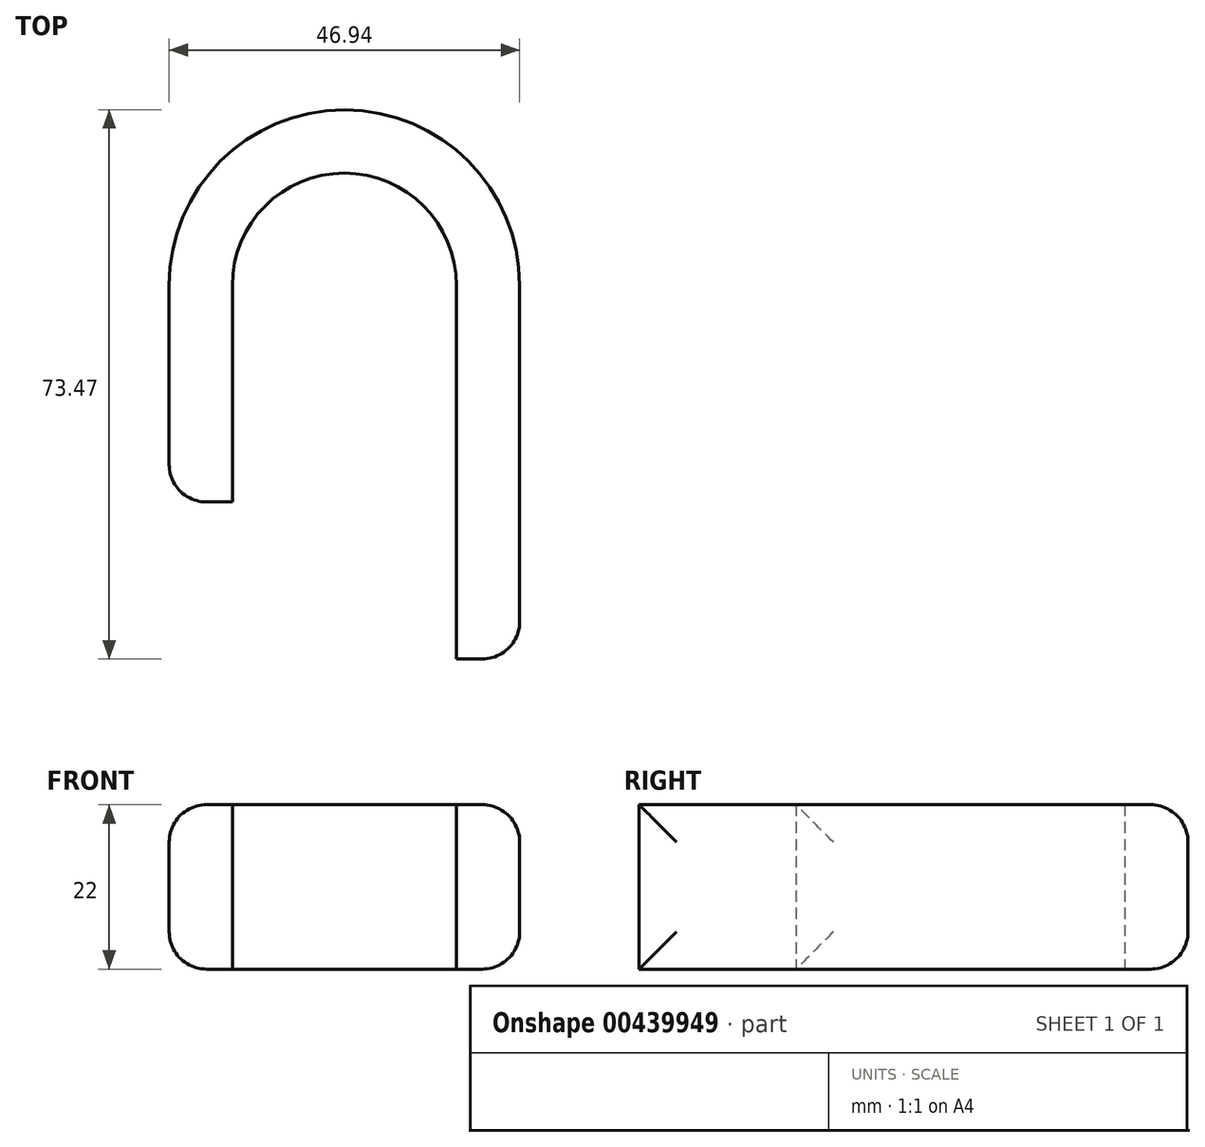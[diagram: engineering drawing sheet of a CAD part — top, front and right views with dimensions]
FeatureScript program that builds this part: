
annotation { "Feature Type Name" : "Feature", "Feature Type Description" : "" }
export const myFeature = defineFeature(function(context is Context, id is Id, definition is map)
    precondition{}
    {
        {
            var Q0;
            Q0=qCreatedBy(makeId("Top.planeOp"),FACE);
            var sketch = newSketch(context, id + "F0", { "sketchPlane" : qUnion([Q0])});
            skCircle(sketch, "E0", {"center": v(0, 0) * mm, "radius": 23.47 * mm});
            skLineSegment(sketch, "E1", {"start": v(-23.47, 0) * mm, "end": v(-23.47, -29) * mm});
            skLineSegment(sketch, "E2", {"start": v(23.47, 0) * mm, "end": v(23.47, -50) * mm});
            skCircle(sketch, "E3", {"center": v(0, 0) * mm, "radius": 15 * mm});
            skLineSegment(sketch, "E4", {"start": v(-15, 0) * mm, "end": v(-15, -29) * mm});
            skLineSegment(sketch, "E5", {"start": v(15, 0) * mm, "end": v(15, -50) * mm});
            skLineSegment(sketch, "E6", {"start": v(-23.47, -29) * mm, "end": v(-15, -29) * mm});
            skLineSegment(sketch, "E7", {"start": v(15, -50) * mm, "end": v(23.47, -50) * mm});
            skSolve(sketch);
        }
        {
            var Q0;
            {var subQ0=sQuery(id+"F0.wireOp",EDGE,"E1");Q0=makeQuery(id+"F0.imprint","IMPRINT",FACE,{"disambiguationData":[TD([[makeQuery(id+"F0.imprint","IMPRINT",EDGE,{"derivedFrom":subQ0}),1.0]])]});}
            var Q1;
            {var subQ0=sQuery(id+"F0.wireOp",EDGE,"E2");Q1=makeQuery(id+"F0.imprint","IMPRINT",FACE,{"disambiguationData":[TD([[makeQuery(id+"F0.imprint","IMPRINT",EDGE,{"derivedFrom":subQ0}),-1.0]])]});}
            var Q2;
            {var subQ0=sQuery(id+"F0.wireOp",EDGE,"E0");var subQ8=makeQuery(id+"F0.imprint","INTERSECT",VERTEX,{"derivedFrom":[subQ0,sQuery(id+"F0.wireOp",EDGE,"E1")]});Q2=makeQuery(id+"F0.imprint","IMPRINT",FACE,{"disambiguationData":[TD([[makeQuery(id+"F0.imprint","IMPRINT",EDGE,{"disambiguationData":[TD([[subQ8,1.0]])],"derivedFrom":subQ0}),1.0]])]});}
            extrude(context, id + "F1", {"entities" : qUnion([Q0, Q1, Q2]), "depth" : 22 * mm});
        }
        {
            var Q0;
            Q0=makeQuery(id+"F1.opExtrude","SWEPT_EDGE",EDGE,{"disambiguationData":[OSD([sQuery(id+"F0.wireOp",EDGE,"E2"),sQuery(id+"F0.wireOp",EDGE,"E7")])]});
            var Q1;
            Q1=makeQuery(id+"F1.opExtrude","CAP_EDGE",EDGE,{"disambiguationData":[OSD([sQuery(id+"F0.wireOp",EDGE,"E1")])],"isStart":false});
            var Q2;
            Q2=makeQuery(id+"F1.opExtrude","CAP_EDGE",EDGE,{"disambiguationData":[OSD([sQuery(id+"F0.wireOp",EDGE,"E2")])],"isStart":true});
            var Q3;
            Q3=makeQuery(id+"F1.opExtrude","SWEPT_EDGE",EDGE,{"disambiguationData":[OSD([sQuery(id+"F0.wireOp",EDGE,"E1"),sQuery(id+"F0.wireOp",EDGE,"E6")])]});
            fillet(context, id + "F2", {"entities" : qUnion([Q0, Q1, Q2, Q3]), "radius" : 5 * mm, "tangentPropagation" : true, "allowEdgeOverflow" : false});
        }
    });
